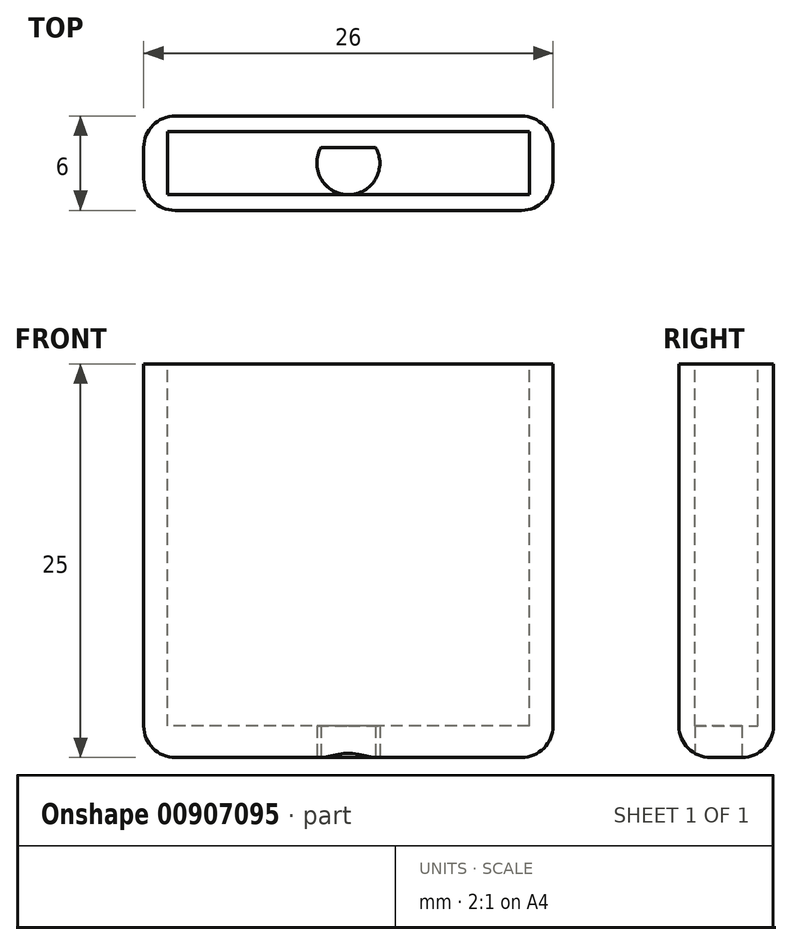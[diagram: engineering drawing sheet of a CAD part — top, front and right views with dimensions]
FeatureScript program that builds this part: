
annotation { "Feature Type Name" : "Feature", "Feature Type Description" : "" }
export const myFeature = defineFeature(function(context is Context, id is Id, definition is map)
    precondition{}
    {
        {
            var Q0;
            Q0=qCreatedBy(makeId("Top.planeOp"),FACE);
            var sketch = newSketch(context, id + "F0", { "sketchPlane" : qUnion([Q0])});
            skLineSegment(sketch, "E0.bottom", {"start": v(13, -3) * mm, "end": v(-13, -3) * mm});
            skLineSegment(sketch, "E0.top", {"start": v(13, 3) * mm, "end": v(-13, 3) * mm});
            skLineSegment(sketch, "E0.left", {"start": v(13, -3) * mm, "end": v(13, 3) * mm});
            skLineSegment(sketch, "E0.right", {"start": v(-13, -3) * mm, "end": v(-13, 3) * mm});
            skPoint(sketch, "E0.middle", {"position": v(0, 0) * mm});
            skSolve(sketch);
        }
        {
            var Q0;
            Q0=makeQuery(id+"F0.imprint","IMPRINT",FACE,{"disambiguationData":[TD([[makeQuery(id+"F0.imprint","IMPRINT",EDGE,{"derivedFrom":sQuery(id+"F0.wireOp",EDGE,"E0.bottom")}),-1.0]])]});
            extrude(context, id + "F1", {"entities" : qUnion([Q0]), "depth" : 20 * mm, "offsetDistance" : 25 * mm});
        }
        {
            var Q0;
            Q0=makeQuery(id+"F1.opExtrude","CAP_FACE",FACE,{"disambiguationData":[OSD([sQuery(id+"F0.wireOp",EDGE,"E0.bottom"),sQuery(id+"F0.wireOp",EDGE,"E0.top"),sQuery(id+"F0.wireOp",EDGE,"E0.left"),sQuery(id+"F0.wireOp",EDGE,"E0.right")])],"isStart":false});
            var sketch = newSketch(context, id + "F2", { "sketchPlane" : qUnion([Q0])});
            skLineSegment(sketch, "E1.bottom", {"start": v(11.5, -2) * mm, "end": v(-11.5, -2) * mm});
            skLineSegment(sketch, "E1.top", {"start": v(11.5, 2) * mm, "end": v(-11.5, 2) * mm});
            skLineSegment(sketch, "E1.left", {"start": v(11.5, -2) * mm, "end": v(11.5, 2) * mm});
            skLineSegment(sketch, "E1.right", {"start": v(-11.5, -2) * mm, "end": v(-11.5, 2) * mm});
            skPoint(sketch, "E1.middle", {"position": v(0, 0) * mm});
            skSolve(sketch);
        }
        {
            var Q0;
            Q0=makeQuery(id+"F2.imprint","IMPRINT",FACE,{"disambiguationData":[TD([[makeQuery(id+"F2.imprint","IMPRINT",EDGE,{"derivedFrom":sQuery(id+"F2.wireOp",EDGE,"E1.bottom")}),-1.0]])]});
            extrude(context, id + "F3", {"entities" : qUnion([Q0]), "operationType" : NewBodyOperationType.REMOVE, "oppositeDirection" : true, "depth" : 18 * mm, "offsetDistance" : 25 * mm});
        }
        {
            var Q0;
            Q0=makeQuery(id+"F1.opExtrude","SWEPT_EDGE",EDGE,{"disambiguationData":[OSD([sQuery(id+"F0.wireOp",EDGE,"E0.top"),sQuery(id+"F0.wireOp",EDGE,"E0.right")])]});
            var Q1;
            Q1=makeQuery(id+"F1.opExtrude","SWEPT_EDGE",EDGE,{"disambiguationData":[OSD([sQuery(id+"F0.wireOp",EDGE,"E0.bottom"),sQuery(id+"F0.wireOp",EDGE,"E0.right")])]});
            var Q2;
            Q2=makeQuery(id+"F1.opExtrude","CAP_FACE",FACE,{"disambiguationData":[OSD([sQuery(id+"F0.wireOp",EDGE,"E0.bottom"),sQuery(id+"F0.wireOp",EDGE,"E0.top"),sQuery(id+"F0.wireOp",EDGE,"E0.left"),sQuery(id+"F0.wireOp",EDGE,"E0.right")])],"isStart":true});
            var Q3;
            Q3=makeQuery(id+"F1.opExtrude","SWEPT_EDGE",EDGE,{"disambiguationData":[OSD([sQuery(id+"F0.wireOp",EDGE,"E0.bottom"),sQuery(id+"F0.wireOp",EDGE,"E0.left")])]});
            var Q4;
            Q4=makeQuery(id+"F1.opExtrude","SWEPT_EDGE",EDGE,{"disambiguationData":[OSD([sQuery(id+"F0.wireOp",EDGE,"E0.top"),sQuery(id+"F0.wireOp",EDGE,"E0.left")])]});
            fillet(context, id + "F4", {"entities" : qUnion([Q0, Q1, Q2, Q3, Q4]), "radius" : 2 * mm, "tangentPropagation" : true, "allowEdgeOverflow" : false});
        }
        {
            var Q0;
            Q0=makeQuery(id+"F1.opExtrude","CAP_FACE",FACE,{"disambiguationData":[OSD([sQuery(id+"F0.wireOp",EDGE,"E0.bottom"),sQuery(id+"F0.wireOp",EDGE,"E0.top"),sQuery(id+"F0.wireOp",EDGE,"E0.left"),sQuery(id+"F0.wireOp",EDGE,"E0.right")])],"isStart":true});
            var sketch = newSketch(context, id + "F5", { "sketchPlane" : qUnion([Q0])});
            skCircle(sketch, "E2", {"center": v(0, 0) * mm, "radius": 2 * mm});
            skSolve(sketch);
        }
        {
            var Q0;
            {var subQ0=sQuery(id+"F5.wireOp",EDGE,"E2");var subQ1=sQuery(id+"F0.wireOp",EDGE,"E0.top");var subQ2=sQuery(id+"F0.wireOp",EDGE,"E0.bottom");var subQ3=makeQuery(id+"F1.opExtrude","CAP_FACE",FACE,{"disambiguationData":[OSD([subQ2,subQ1,sQuery(id+"F0.wireOp",EDGE,"E0.left"),sQuery(id+"F0.wireOp",EDGE,"E0.right")])],"isStart":true});var subQ4=makeQuery(id+"F4.opFillet","BLEND_EDGE",EDGE,{"blendedFrom":[makeQuery(id+"F1.opExtrude","CAP_EDGE",EDGE,{"disambiguationData":[OSD([subQ2])],"isStart":true}),subQ3],"blendedInto":[subQ3]});var subQ5=makeQuery(id+"F5.imprint","INTERSECT",VERTEX,{"disambiguationData":[OD(0.0)],"derivedFrom":[subQ4,subQ0]});Q0=makeQuery(id+"F5.imprint","IMPRINT",FACE,{"disambiguationData":[TD([[makeQuery(id+"F5.imprint","IMPRINT",EDGE,{"disambiguationData":[TD([[subQ5,-1.0]])],"derivedFrom":subQ0}),1.0]])]});}
            var Q1;
            {var subQ0=sQuery(id+"F5.wireOp",EDGE,"E2");var subQ1=sQuery(id+"F0.wireOp",EDGE,"E0.top");var subQ2=makeQuery(id+"F4.opFillet","BLEND_EDGE",EDGE,{"blendedFrom":[makeQuery(id+"F1.opExtrude","CAP_EDGE",EDGE,{"disambiguationData":[OSD([subQ1])],"isStart":true}),makeQuery(id+"F1.opExtrude","CAP_FACE",FACE,{"disambiguationData":[OSD([sQuery(id+"F0.wireOp",EDGE,"E0.bottom"),subQ1,sQuery(id+"F0.wireOp",EDGE,"E0.left"),sQuery(id+"F0.wireOp",EDGE,"E0.right")])],"isStart":true})],"blendedInto":[makeQuery(id+"F1.opExtrude","CAP_FACE",FACE,{"disambiguationData":[OSD([sQuery(id+"F0.wireOp",EDGE,"E0.bottom"),subQ1,sQuery(id+"F0.wireOp",EDGE,"E0.left"),sQuery(id+"F0.wireOp",EDGE,"E0.right")])],"isStart":true})]});var subQ3=makeQuery(id+"F5.imprint","INTERSECT",VERTEX,{"disambiguationData":[OD(0.0)],"derivedFrom":[subQ2,subQ0]});Q1=makeQuery(id+"F5.imprint","IMPRINT",FACE,{"disambiguationData":[TD([[makeQuery(id+"F5.imprint","IMPRINT",EDGE,{"disambiguationData":[TD([[subQ3,-1.0]])],"derivedFrom":subQ0}),1.0]])]});}
            var Q2;
            {var subQ0=sQuery(id+"F5.wireOp",EDGE,"E2");var subQ1=sQuery(id+"F0.wireOp",EDGE,"E0.bottom");var subQ2=makeQuery(id+"F4.opFillet","BLEND_EDGE",EDGE,{"blendedFrom":[makeQuery(id+"F1.opExtrude","CAP_EDGE",EDGE,{"disambiguationData":[OSD([subQ1])],"isStart":true}),makeQuery(id+"F1.opExtrude","CAP_FACE",FACE,{"disambiguationData":[OSD([subQ1,sQuery(id+"F0.wireOp",EDGE,"E0.top"),sQuery(id+"F0.wireOp",EDGE,"E0.left"),sQuery(id+"F0.wireOp",EDGE,"E0.right")])],"isStart":true})],"blendedInto":[makeQuery(id+"F1.opExtrude","CAP_FACE",FACE,{"disambiguationData":[OSD([subQ1,sQuery(id+"F0.wireOp",EDGE,"E0.top"),sQuery(id+"F0.wireOp",EDGE,"E0.left"),sQuery(id+"F0.wireOp",EDGE,"E0.right")])],"isStart":true})]});var subQ3=makeQuery(id+"F5.imprint","INTERSECT",VERTEX,{"disambiguationData":[OD(0.0)],"derivedFrom":[subQ2,subQ0]});Q2=makeQuery(id+"F5.imprint","IMPRINT",FACE,{"disambiguationData":[TD([[makeQuery(id+"F5.imprint","IMPRINT",EDGE,{"disambiguationData":[TD([[subQ3,1.0]])],"derivedFrom":subQ0}),1.0]])]});}
            extrude(context, id + "F6", {"entities" : qUnion([Q0, Q1, Q2]), "operationType" : NewBodyOperationType.REMOVE, "oppositeDirection" : true, "depth" : 25 * mm, "offsetDistance" : 25 * mm});
        }
        {
            var Q0;
            Q0=makeQuery(id+"F1.opExtrude","CAP_FACE",FACE,{"disambiguationData":[OSD([sQuery(id+"F0.wireOp",EDGE,"E0.bottom"),sQuery(id+"F0.wireOp",EDGE,"E0.top"),sQuery(id+"F0.wireOp",EDGE,"E0.left"),sQuery(id+"F0.wireOp",EDGE,"E0.right")])],"isStart":false});
            extrude(context, id + "F7", {"entities" : qUnion([Q0]), "operationType" : NewBodyOperationType.ADD, "depth" : 5 * mm, "offsetDistance" : 25 * mm});
        }
    });
